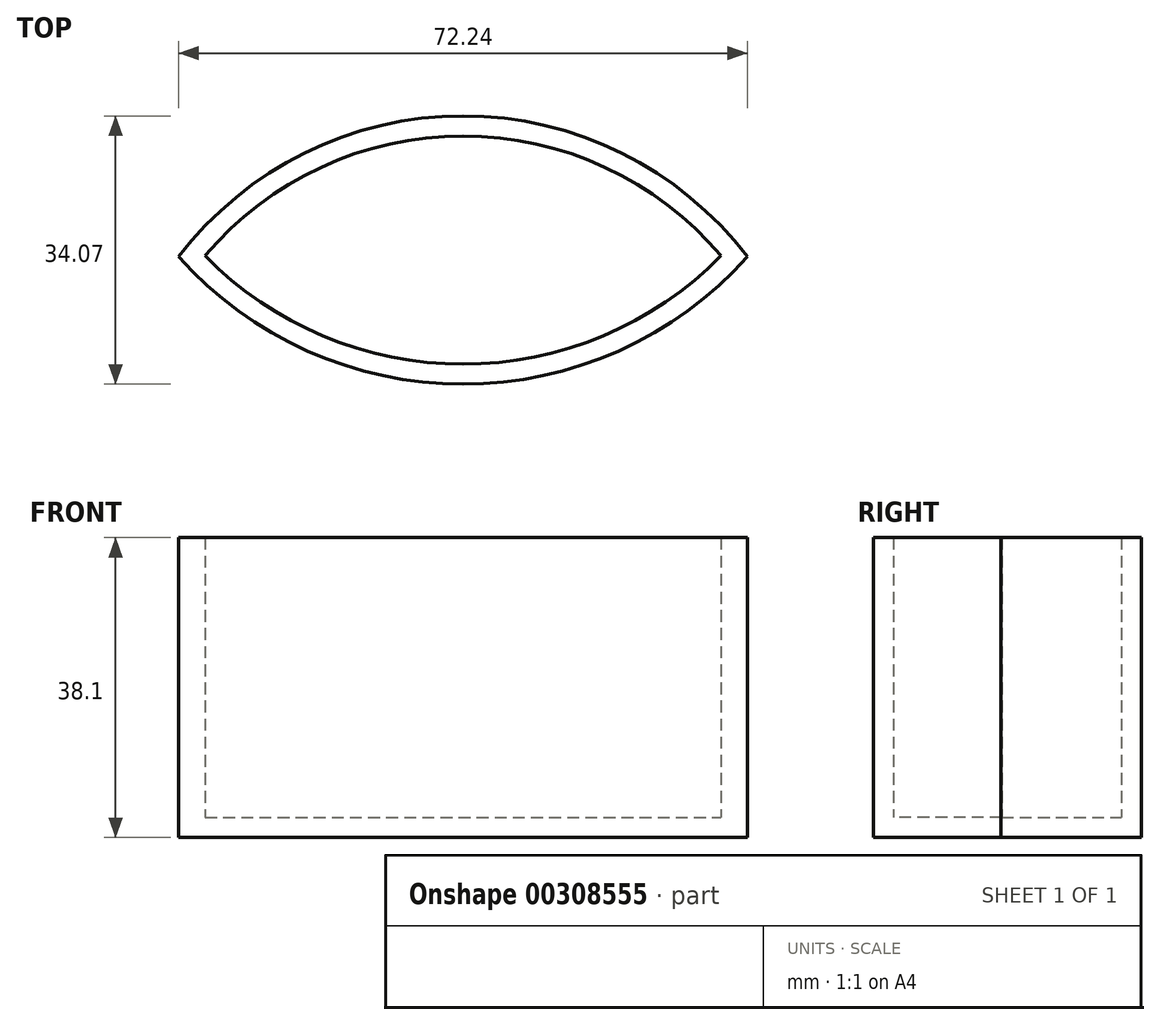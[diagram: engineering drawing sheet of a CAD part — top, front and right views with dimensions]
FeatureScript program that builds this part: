
annotation { "Feature Type Name" : "Feature", "Feature Type Description" : "" }
export const myFeature = defineFeature(function(context is Context, id is Id, definition is map)
    precondition{}
    {
        {
            var Q0;
            Q0=qCreatedBy(makeId("Top.planeOp"),FACE);
            var sketch = newSketch(context, id + "F0", { "sketchPlane" : qUnion([Q0])});
            skArc(sketch, "E0", {"start": v(29.87, 0) * mm, "mid": v(-6.25, 17.9) * mm, "end": v(-42.37, 0) * mm});
            skArc(sketch, "E1", {"start": v(-42.37, 0) * mm, "mid": v(-6.25, -16.18) * mm, "end": v(29.87, 0) * mm});
            skSolve(sketch);
        }
        {
            var Q0;
            Q0=makeQuery(id+"F0.imprint","IMPRINT",FACE,{"disambiguationData":[TD([[makeQuery(id+"F0.imprint","IMPRINT",EDGE,{"derivedFrom":sQuery(id+"F0.wireOp",EDGE,"E0")}),1.0]])]});
            extrude(context, id + "F1", {"entities" : qUnion([Q0]), "depth" : 38.1 * mm});
        }
        {
            var Q0;
            Q0=makeQuery(id+"F1.opExtrude","CAP_FACE",FACE,{"disambiguationData":[OSD([sQuery(id+"F0.wireOp",EDGE,"E0"),sQuery(id+"F0.wireOp",EDGE,"E1")])],"isStart":false});
            shell(context, id + "F2", {"entities" : qUnion([Q0]), "thickness" : 2.54 * mm});
        }
    });
